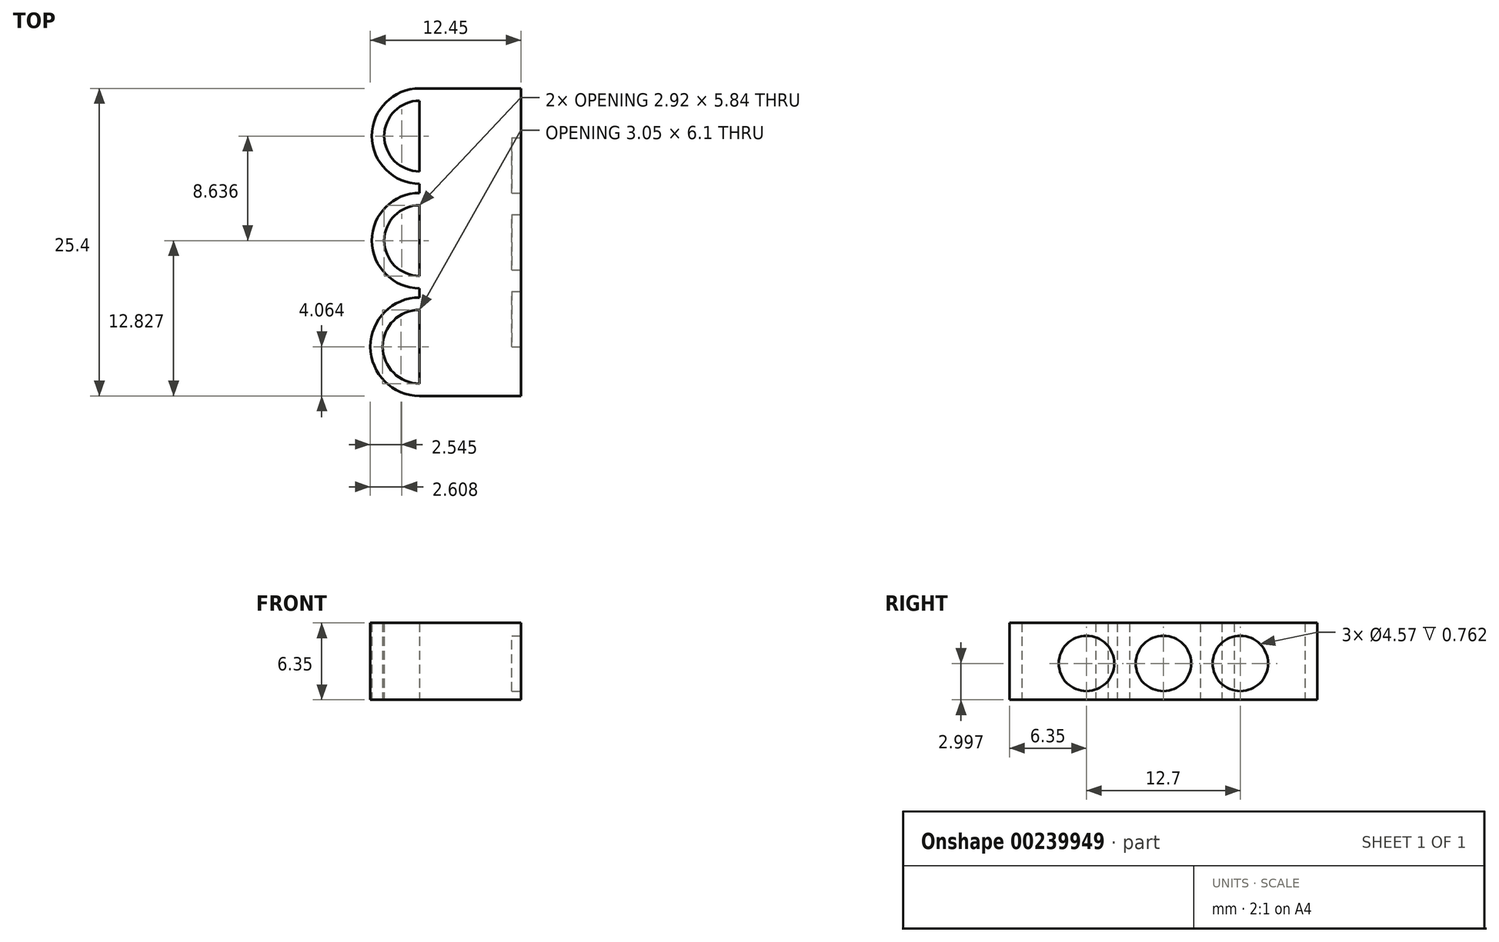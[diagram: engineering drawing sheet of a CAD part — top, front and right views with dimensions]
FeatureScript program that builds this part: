
annotation { "Feature Type Name" : "Feature", "Feature Type Description" : "" }
export const myFeature = defineFeature(function(context is Context, id is Id, definition is map)
    precondition{}
    {
        {
            var Q0;
            Q0=qCreatedBy(makeId("Top.planeOp"),FACE);
            var sketch = newSketch(context, id + "F0", { "sketchPlane" : qUnion([Q0])});
            skLineSegment(sketch, "E0.bottom", {"start": v(-4.2, 25.4) * mm, "end": v(4.2, 25.4) * mm});
            skLineSegment(sketch, "E0.top", {"start": v(-4.2, 0) * mm, "end": v(4.2, 0) * mm});
            skLineSegment(sketch, "E0.left", {"start": v(-4.2, 25.4) * mm, "end": v(-4.2, 0) * mm});
            skLineSegment(sketch, "E0.right", {"start": v(4.2, 25.4) * mm, "end": v(4.2, 0) * mm});
            skArc(sketch, "E1", {"start": v(-4.2, 25.4) * mm, "mid": v(-8.13, 21.46) * mm, "end": v(-4.2, 17.53) * mm});
            skArc(sketch, "E2", {"start": v(-4.2, 16.76) * mm, "mid": v(-8.13, 12.83) * mm, "end": v(-4.2, 8.9) * mm});
            skArc(sketch, "E3", {"start": v(-4.2, 8.13) * mm, "mid": v(-8.25, 4.06) * mm, "end": v(-4.2, 0) * mm});
            skArc(sketch, "E4.0", {"start": v(-4.2, 24.38) * mm, "mid": v(-7.11, 21.46) * mm, "end": v(-4.2, 18.54) * mm});
            skArc(sketch, "E5.0", {"start": v(-4.2, 15.75) * mm, "mid": v(-7.11, 12.83) * mm, "end": v(-4.2, 9.9) * mm});
            skArc(sketch, "E6.0", {"start": v(-4.2, 7.11) * mm, "mid": v(-7.24, 4.06) * mm, "end": v(-4.2, 1.02) * mm});
            skSolve(sketch);
        }
        {
            var Q0;
            {var subQ4=sQuery(id+"F0.wireOp",EDGE,"E0.bottom");Q0=makeQuery(id+"F0.imprint","IMPRINT",FACE,{"disambiguationData":[TD([[makeQuery(id+"F0.imprint","IMPRINT",EDGE,{"derivedFrom":subQ4}),-1.0]])]});}
            var Q1;
            {var subQ0=sQuery(id+"F0.wireOp",EDGE,"E2");Q1=makeQuery(id+"F0.imprint","IMPRINT",FACE,{"disambiguationData":[TD([[makeQuery(id+"F0.imprint","IMPRINT",EDGE,{"derivedFrom":subQ0}),1.0]])]});}
            var Q2;
            {var subQ0=sQuery(id+"F0.wireOp",EDGE,"E3");Q2=makeQuery(id+"F0.imprint","IMPRINT",FACE,{"disambiguationData":[TD([[makeQuery(id+"F0.imprint","IMPRINT",EDGE,{"derivedFrom":subQ0}),1.0]])]});}
            var Q3;
            {var subQ0=sQuery(id+"F0.wireOp",EDGE,"E1");Q3=makeQuery(id+"F0.imprint","IMPRINT",FACE,{"disambiguationData":[TD([[makeQuery(id+"F0.imprint","IMPRINT",EDGE,{"derivedFrom":subQ0}),1.0]])]});}
            extrude(context, id + "F1", {"entities" : qUnion([Q0, Q1, Q2, Q3]), "depth" : 6.35 * mm});
        }
        {
            var Q0;
            Q0=makeQuery(id+"F1.opExtrude","SWEPT_FACE",FACE,{"disambiguationData":[OSD([sQuery(id+"F0.wireOp",EDGE,"E0.right")])]});
            var sketch = newSketch(context, id + "F2", { "sketchPlane" : qUnion([Q0])});
            skCircle(sketch, "E7", {"center": v(6.35, 3) * mm, "radius": 2.29 * mm});
            skCircle(sketch, "E8", {"center": v(12.7, 3) * mm, "radius": 2.29 * mm});
            skCircle(sketch, "E9", {"center": v(19.05, 3) * mm, "radius": 2.29 * mm});
            skSolve(sketch);
        }
        {
            var Q0;
            Q0=makeQuery(id+"F2.imprint","IMPRINT",FACE,{"disambiguationData":[TD([[makeQuery(id+"F2.imprint","IMPRINT",EDGE,{"derivedFrom":sQuery(id+"F2.wireOp",EDGE,"E7")}),1.0]])]});
            var Q1;
            Q1=makeQuery(id+"F2.imprint","IMPRINT",FACE,{"disambiguationData":[TD([[makeQuery(id+"F2.imprint","IMPRINT",EDGE,{"derivedFrom":sQuery(id+"F2.wireOp",EDGE,"E8")}),1.0]])]});
            var Q2;
            Q2=makeQuery(id+"F2.imprint","IMPRINT",FACE,{"disambiguationData":[TD([[makeQuery(id+"F2.imprint","IMPRINT",EDGE,{"derivedFrom":sQuery(id+"F2.wireOp",EDGE,"E9")}),1.0]])]});
            extrude(context, id + "F3", {"entities" : qUnion([Q0, Q1, Q2]), "operationType" : NewBodyOperationType.REMOVE, "oppositeDirection" : true, "depth" : 0.76 * mm});
        }
    });
